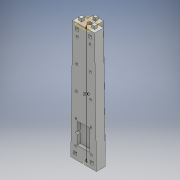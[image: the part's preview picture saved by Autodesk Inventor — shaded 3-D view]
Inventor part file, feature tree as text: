
AUTODESK INVENTOR PART (.ipt)
format: ipt  version: 2017 (Build 210142000, 142)  size: 528,384 bytes
history: native  units: mm
features: sketch x41, extrude x33, chamfer x10, loft x2, plane x1, other x1, hole x1
ambient origin geometry x8: Origin, YZ Plane, XZ Plane, XY Plane, X Axis, Y Axis, Z Axis, Center Point
bodies: Solid1 (feature_tree)
feature tree (89):
  sketch  "Sketch1"  dims[d0=43.0mm d1=15.0mm]
  sketch  "Sketch2"  dims[d2=12.5mm d3=23.0mm]
  sketch  "Sketch3"  dims[d4=10.0mm d5=200.0mm]
  plane  "Work Plane1"
  sketch  "Sketch4"  dims[d6=37.0mm d7=15.0mm]
  sketch  "Sketch5"  dims[d8=12.5mm d9=17.0mm]
  loft  "Loft1"
  loft  "Loft2"
  other  "Work Point1"
  sketch  "Sketch7"  dims[d10=10.0mm d11=0.0mm d12=90.0deg]
  sketch  "Sketch8"  dims[d13=0.0mm d14=90.0deg d15=0.0mm d16=90.0deg]
  extrude  "Extrusion10"  Depth=200.0mm
  extrude  "Extrusion11"  Depth=15.0mm
  sketch  "Sketch15"  dims[d17=0.0mm d18=90.0deg d30=5.5mm]
  sketch  "Sketch16"  dims[d31=5.5mm d32=5.5mm]
  sketch  "Sketch18"  dims[d66=6.0mm d67=0.0mm d78=2.0mm]
  sketch  "Sketch19"  dims[d79=0.0mm d80=2.0mm]
  sketch  "Sketch20"  dims[d81=0.0mm d82=1.2mm]
  extrude  "Extrusion17"  Depth=17.0mm
  extrude  "Extrusion18"  TaperAngle=0.0deg  [1 undecoded]
  extrude  "Extrusion19"  TaperAngle=0.0deg  [1 undecoded]
  extrude  "Extrusion20"  Depth=5.5mm
  extrude  "Extrusion21"  Depth=5.5mm
  extrude  "Extrusion22"  Depth=6.0mm TaperAngle=0.0deg
  extrude  "Extrusion23"  Depth=2.0mm
  extrude  "Extrusion24"  Depth=2.0mm
  extrude  "Extrusion25"  Depth=1.2mm
  extrude  "Extrusion26"  Depth=6.6mm TaperAngle=0.0deg
  extrude  "Extrusion27"  Depth=2.8mm
  extrude  "Extrusion28"  Depth=2.0mm
  extrude  "Extrusion29"  TaperAngle=0.0deg  [1 undecoded]
  extrude  "Extrusion30"  TaperAngle=0.0deg  [1 undecoded]
  extrude  "Extrusion31"  Depth=1.2mm
  extrude  "Extrusion32"  Depth=2.8mm
  extrude  "Extrusion33"  Depth=8.0mm TaperAngle=0.0deg
  extrude  "Extrusion34"  Depth=1.2mm
  extrude  "Extrusion35"  Depth=2.8mm
  extrude  "Extrusion36"  Depth=8.0mm TaperAngle=0.0deg
  chamfer  "Chamfer1"  Distance=6.6mm
  chamfer  "Chamfer2"  Distance=8.0mm
  chamfer  "Chamfer3"  Distance=6.6mm
  chamfer  "Chamfer4"  Distance=8.0mm
  chamfer  "Chamfer5"  Distance=6.6mm
  chamfer  "Chamfer6"  Distance=8.0mm
  chamfer  "Chamfer7"  Distance=1.2mm
  chamfer  "Chamfer8"  Distance=6.6mm
  chamfer  "Chamfer9"  Distance=2.8mm
  chamfer  "Chamfer10"  Distance=2.8mm
  hole  "Hole2"  [1 undecoded]
  sketch  "Sketch37"  dims[d119=1.2mm]
  sketch  "Sketch38"  dims[d120=1.2mm d121=6.6mm d122=0.0mm]
  sketch  "Sketch39"  dims[d123=2.8mm]
  sketch  "Sketch40"  dims[d124=2.8mm d125=8.0mm d126=0.0mm]
  sketch  "Sketch41"  dims[d127=2.0mm]
  extrude  "Extrusion37"  Depth=2.0mm
  extrude  "Extrusion38"  Depth=1.2mm
  extrude  "Extrusion39"  Depth=1.2mm
  extrude  "Extrusion40"  Depth=6.6mm TaperAngle=0.0deg
  extrude  "Extrusion41"  Depth=2.8mm
  extrude  "Extrusion42"  Depth=2.8mm
  extrude  "Extrusion43"  Depth=8.0mm TaperAngle=0.0deg
  sketch  "Sketch45"  dims[d133=2.8mm]
  sketch  "Sketch47"  dims[d134=2.8mm d135=8.0mm d136=0.0mm]
  extrude  "Extrusion44"  Depth=2.0mm
  extrude  "Extrusion45"  TaperAngle=180.0deg  [1 undecoded]
  extrude  "Extrusion46"  Depth=1.2mm
  extrude  "Extrusion47"  Depth=1.2mm
  sketch  "Sketch17"  dims[d33=5.5mm d64=6.0mm d65=0.0mm]
  sketch  "Sketch21"  dims[d83=1.2mm d84=6.6mm d85=0.0mm]
  sketch  "Sketch22"  dims[d86=2.8mm d87=2.8mm]
  sketch  "Sketch23"  dims[d88=8.0mm d89=0.0mm d90=2.0mm]
  sketch  "Sketch24"  dims[d91=2.0mm d92=0.0mm]
  sketch  "Sketch26"  dims[d93=2.0mm d94=0.0mm]
  sketch  "Sketch27"  dims[d95=1.2mm d96=1.2mm]
  sketch  "Sketch28"  dims[d97=6.6mm d98=0.0mm d99=2.8mm]
  sketch  "Sketch29"  dims[d100=2.8mm d101=8.0mm d102=0.0mm]
  sketch  "Sketch30"  dims[d103=1.2mm d104=1.2mm]
  sketch  "Sketch31"  dims[d105=6.6mm d106=0.0mm d107=2.8mm]
  sketch  "Sketch32"  dims[d108=2.8mm d109=8.0mm d110=0.0mm]
  sketch  "Sketch33"  dims[d111=1.2mm]
  sketch  "Sketch34"  dims[d112=1.2mm d113=6.6mm d114=0.0mm]
  sketch  "Sketch35"  dims[d115=2.8mm]
  sketch  "Sketch36"  dims[d116=2.8mm d117=8.0mm d118=0.0mm]
  sketch  "Sketch42"  dims[d128=180.0deg]
  sketch  "Sketch43"  dims[d129=1.2mm]
  sketch  "Sketch44"  dims[d130=1.2mm d131=6.6mm d132=0.0mm]
  sketch  "Sketch48"  dims[d137=2.0mm]
  sketch  "Sketch49"  dims[d138=180.0deg]
  sketch  "Sketch50"  dims[d139=1.2mm d140=1.2mm d141=6.6mm d142=0.0mm d143=2.8mm d144=2.8mm d145=8.0mm d146=0.0mm d147=2.0mm d148=1.2mm d149=1.2mm d150=6.6mm d151=0.0mm d152=2.8mm d153=2.8mm d154=8.0mm d155=0.0mm d156=2.0mm d157=180.0deg d158=1.2mm d159=1.2mm d160=6.6mm d161=0.0mm d162=2.8mm d163=2.8mm d164=8.0mm d165=0.0mm d166=2.0mm d167=180.0deg d168=1.2mm d169=1.2mm d170=6.6mm d171=0.0mm d172=2.8mm d173=2.8mm d174=8.0mm d175=0.0mm d176=0.8mm d177=2.0mm d178=45.0deg d179=0.8mm d180=2.0mm d181=45.0deg d182=0.8mm d183=2.0mm d184=45.0deg d185=0.8mm d186=2.0mm d187=45.0deg d188=0.8mm d189=2.0mm d190=45.0deg d191=0.73mm d192=2.0mm d193=45.0deg d194=0.7mm d195=2.0mm d196=45.0deg d197=0.8mm d198=2.0mm d199=45.0deg d200=0.7mm d201=2.0mm d202=45.0deg d203=0.7mm d204=2.0mm d205=45.0deg d206=15.0mm d207=6.4mm d208=6.0mm d209=4.0mm d210=2.0mm d211=90.0deg d212=8.0mm d213=20.594885mm d214=7.5mm d215=9.0mm d216=5.0mm d217=5.0mm d218=7.5mm d219=9.0mm d220=5.0mm d221=5.0mm d222=7.5mm d223=9.0mm d224=5.0mm d225=5.0mm d226=7.5mm d227=9.0mm d228=5.0mm d229=5.0mm d230=6.0mm d231=0.0mm d232=6.0mm d233=0.0mm d234=6.0mm d235=0.0mm d236=6.0mm d237=0.0mm d238=4.5mm d239=4.5mm d240=5.0mm d241=0.0mm d242=21.0mm d243=35.0mm d244=5.0mm d245=0.0mm d246=5.0mm d247=5.0mm d248=0.0mm d249=5.0mm d250=5.0mm d251=5.0mm d252=5.0mm d253=5.0mm d254=0.0mm d255=5.0mm d256=5.0mm d257=5.0mm d258=5.0mm d259=5.0mm d260=0.0mm d261=4.75mm d262=4.75mm d263=5.5mm d264=5.5mm d265=6.0mm d266=0.0mm d267=4.75mm d268=4.75mm d269=5.5mm d270=5.5mm d271=6.0mm d272=0.0mm]
note: 6 required parameter values undecoded (feature->parameter linkage not recoverable at this tier; creation-order binding heuristic only, values carry confidence <= 0.55)
